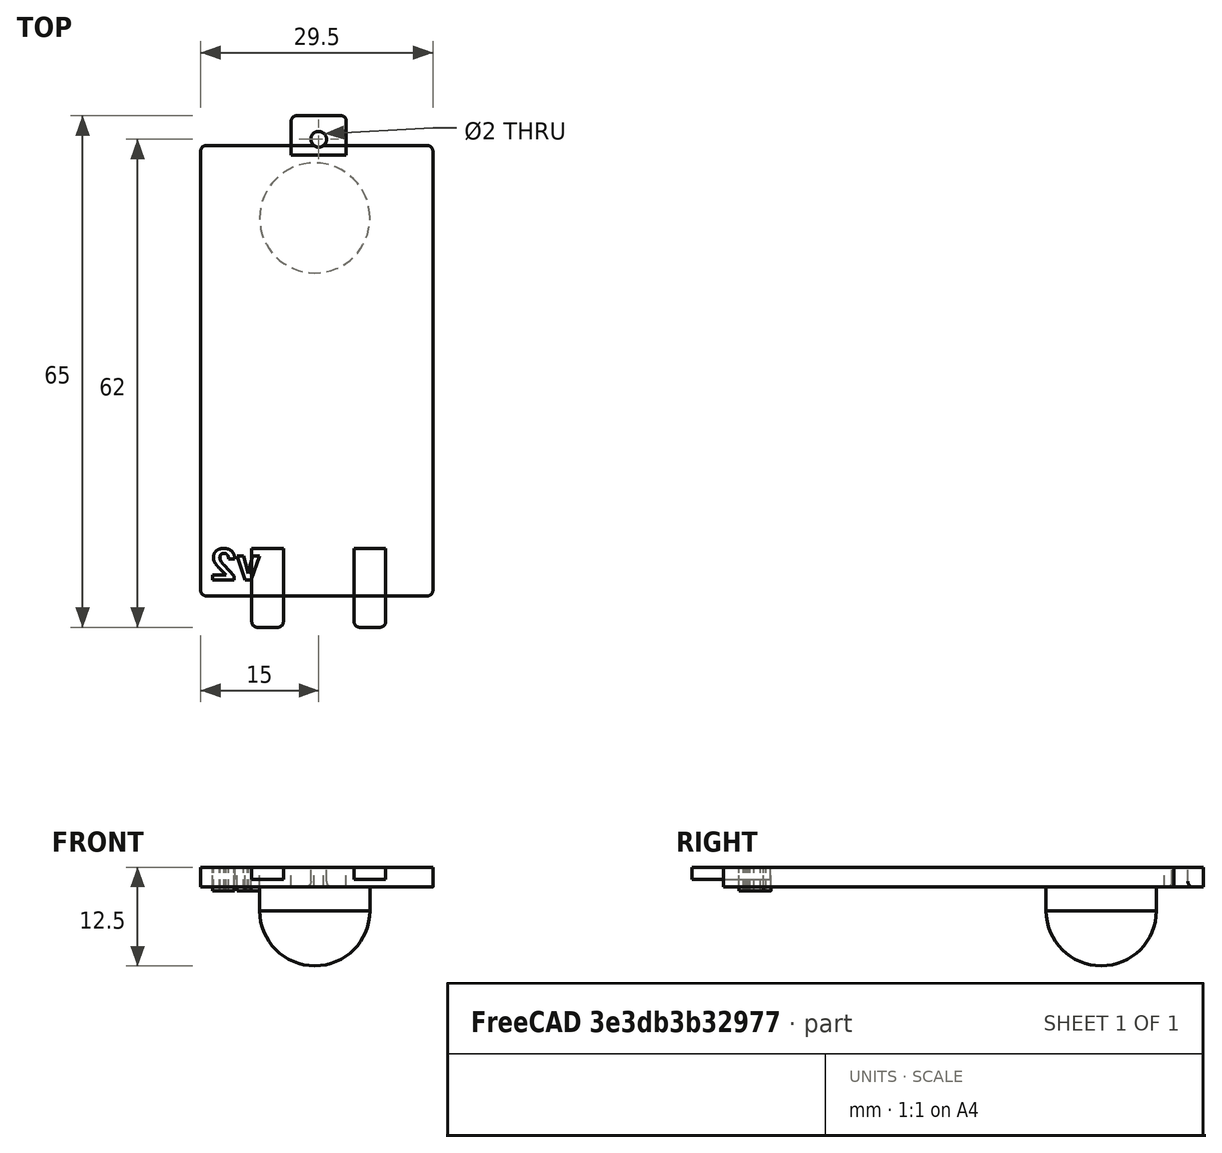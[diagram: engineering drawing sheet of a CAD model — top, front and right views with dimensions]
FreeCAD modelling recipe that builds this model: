
FCSTD DOCUMENT  (FreeCAD 0.16R6712 (Git))
Label: tapa
License: All rights reserved
LicenseURL: http://en.wikipedia.org/wiki/All_rights_reserved
objects: Part::Fillet×8, Part::Box×4, Part::Cylinder×3, Part::Cut×2, Part::Sphere×1, Part::Part2DObjectPython×1, Part::Extrusion×1
note: 20 computed .brp shape members not serialized (recipe doc carries the construction recipe); baked Part::Feature solids carry a one-line shape summary decoded from their .brp

FEATURE [Part::Box] Box  label="base"
  Height = 2.5
  Length = 29.5
  Placement = pos=(0.5,0,0) rot=(0,0,1;0rad)
  Width = 57.2
FEATURE [Part::Box] Box001  label="Cube"
  Height = 1.5
  Length = 4
  Placement = pos=(7,-4,1) rot=(0,0,1;0rad)
  Width = 10
FEATURE [Part::Cylinder] Cylinder001
  Angle = 360
  Height = 2.5
  Placement = pos=(15.5,58,0) rot=(0,0,1;0rad)
  Radius = 1
FEATURE [Part::Cylinder] Cylinder002
  Angle = 360
  Height = 2.5
  Placement = pos=(15.5,58,0) rot=(0,0,1;0rad)
  Radius = 1
FEATURE [Part::Cut] Cut001
  Base = -> Box
  Tool = -> Cylinder002
FEATURE [Part::Box] Box002  label="Cube001"
  Height = 1.5
  Length = 4
  Placement = pos=(20,-4,1) rot=(0,0,1;0rad)
  Width = 10
FEATURE [Part::Box] Box003  label="cargol"
  Height = 2.5
  Length = 7
  Placement = pos=(12,56,0) rot=(0,0,1;0rad)
  Width = 5
FEATURE [Part::Cut] Cut
  Base = -> Box003
  Tool = -> Cylinder001
FEATURE [Part::Fillet] Fillet
  Base = -> Box001
  Edges = 2 edges r=0.7: [Edge1,Edge5]
FEATURE [Part::Fillet] Fillet001
  Base = -> Box002
  Edges = 2 edges r=0.7: [Edge1,Edge5]
FEATURE [Part::Fillet] Fillet002
  Base = -> Cut001
  Edges = 1 edges r=0.7: [Edge6]
FEATURE [Part::Fillet] Fillet003
  Base = -> Fillet002
  Edges = 1 edges r=0.7: [Edge3]
FEATURE [Part::Fillet] Fillet004
  Base = -> Fillet003
  Edges = 1 edges r=0.7: [Edge21]
FEATURE [Part::Fillet] Fillet005
  Base = -> Fillet004
  Edges = 1 edges r=0.7: [Edge25]
FEATURE [Part::Fillet] Fillet006
  Base = -> Cut
  Edges = 2 edges r=0.7: [Edge3,Edge12]
FEATURE [Part::Fillet] Fillet007
  Base = -> Fillet006
  Edges = 1 edges r=0.7: [Edge18]
FEATURE [Part::Sphere] Sphere
  Angle1 = -90
  Angle2 = 0
  Angle3 = 360
  Placement = pos=(15,48,-3) rot=(0,0,1;0rad)
  Radius = 7
FEATURE [Part::Cylinder] Cylinder
  Angle = 360
  Height = 3
  Placement = pos=(15,48,-3) rot=(0,0,1;0rad)
  Radius = 7
FEATURE [Part::Part2DObjectPython] ShapeString  # Draft 2D object (typed FeaturePython)
  FontFile = <userpath>/Desktop/roboto/Roboto-Bold.ttf
  Placement = pos=(8,2,-0.5) rot=(0,1,0;3.14159rad)
  Size = 5
  String = v2
  Tracking = 0
FEATURE [Part::Extrusion] Extrude
  Base = -> ShapeString
  Dir = (0,0,3)
  Solid = false
